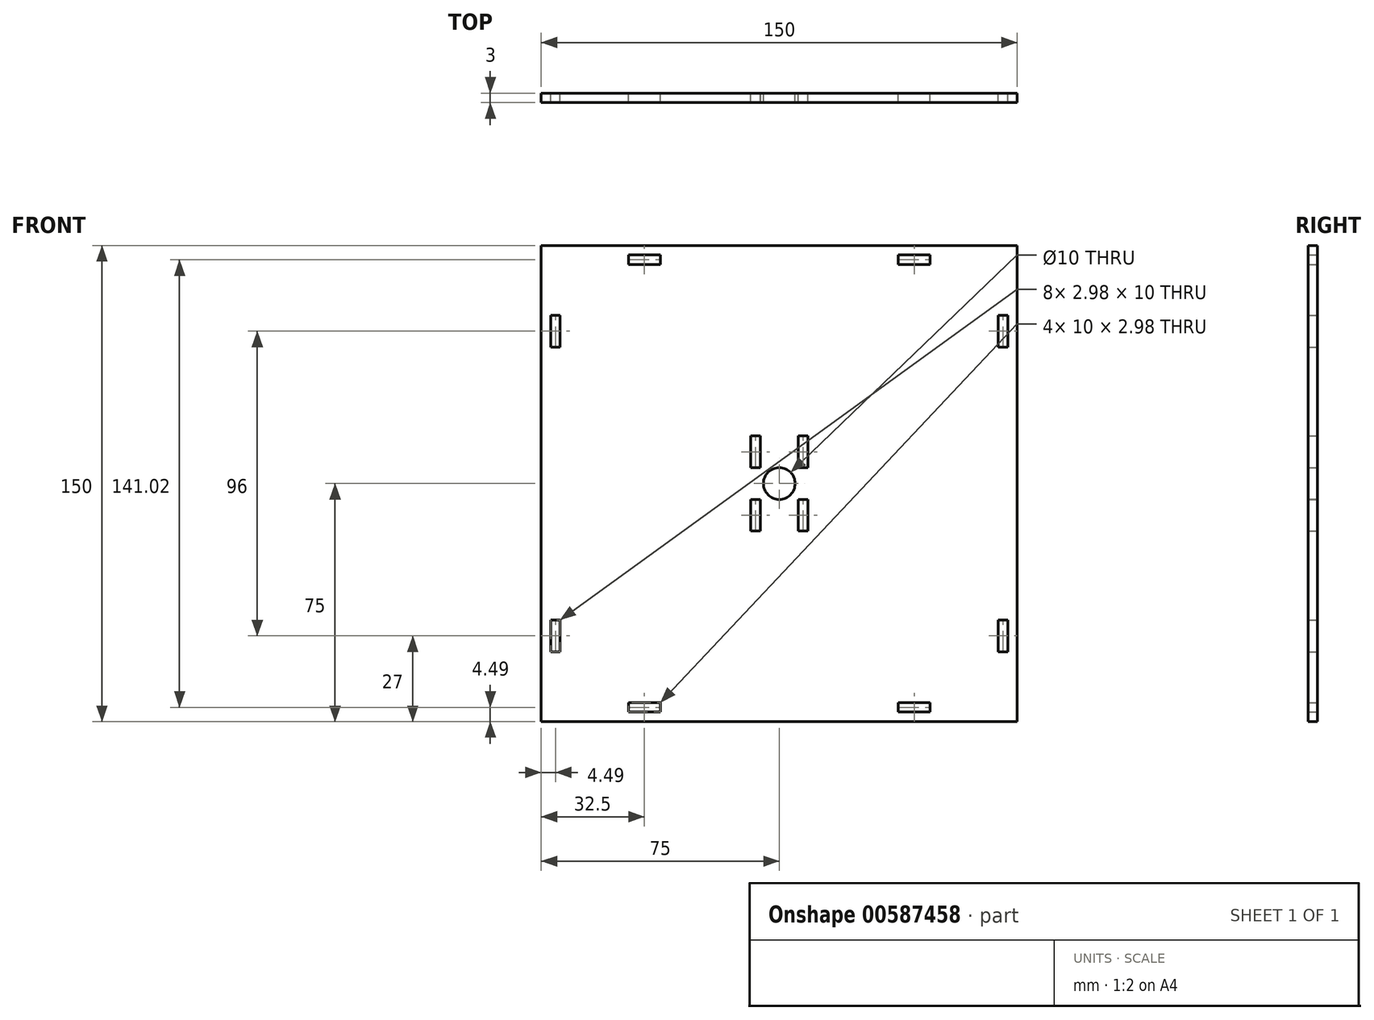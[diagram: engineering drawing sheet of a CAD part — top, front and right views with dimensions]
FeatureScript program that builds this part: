
annotation { "Feature Type Name" : "Feature", "Feature Type Description" : "" }
export const myFeature = defineFeature(function(context is Context, id is Id, definition is map)
    precondition{}
    {
        {
            var Q0;
            Q0=qCreatedBy(makeId("Front.planeOp"),FACE);
            var sketch = newSketch(context, id + "F0", { "sketchPlane" : qUnion([Q0])});
            skLineSegment(sketch, "E0.bottom", {"start": v(-75, 75) * mm, "end": v(75, 75) * mm});
            skLineSegment(sketch, "E0.top", {"start": v(-75, -75) * mm, "end": v(75, -75) * mm});
            skLineSegment(sketch, "E0.left", {"start": v(-75, 75) * mm, "end": v(-75, -75) * mm});
            skLineSegment(sketch, "E0.right", {"start": v(75, 75) * mm, "end": v(75, -75) * mm});
            skLineSegment(sketch, "E1.bottom", {"start": v(-47.5, 72) * mm, "end": v(-37.5, 72) * mm});
            skLineSegment(sketch, "E1.top", {"start": v(-47.5, 69.02) * mm, "end": v(-37.5, 69.02) * mm});
            skLineSegment(sketch, "E1.left", {"start": v(-47.5, 72) * mm, "end": v(-47.5, 69.02) * mm});
            skLineSegment(sketch, "E1.right", {"start": v(-37.5, 72) * mm, "end": v(-37.5, 69.02) * mm});
            skLineSegment(sketch, "E2", {"start": v(0, 75) * mm, "end": v(0, -75) * mm, "construction": true});
            skLineSegment(sketch, "E3", {"start": v(-75, 0) * mm, "end": v(75, 0) * mm, "construction": true});
            skLineSegment(sketch, "E4", {"start": v(-42.5, 72) * mm, "end": v(-42.5, 69.02) * mm, "construction": true});
            skLineSegment(sketch, "E5", {"start": v(-47.5, 70.5) * mm, "end": v(-37.5, 70.5) * mm, "construction": true});
            skLineSegment(sketch, "E6.MirrorCS", {"start": v(47.5, 72) * mm, "end": v(47.5, 69.02) * mm});
            skLineSegment(sketch, "E7.MirrorCS", {"start": v(37.5, 72) * mm, "end": v(37.5, 69.02) * mm});
            skLineSegment(sketch, "E8.MirrorCS", {"start": v(42.5, 72) * mm, "end": v(42.5, 69.02) * mm, "construction": true});
            skLineSegment(sketch, "E9.MirrorCS", {"start": v(47.5, 70.51) * mm, "end": v(37.5, 70.51) * mm, "construction": true});
            skLineSegment(sketch, "E10.MirrorCS", {"start": v(47.5, 69.02) * mm, "end": v(37.5, 69.02) * mm});
            skLineSegment(sketch, "E11.MirrorCS", {"start": v(47.5, 72) * mm, "end": v(37.5, 72) * mm});
            skLineSegment(sketch, "E12.MirrorCS", {"start": v(47.5, -70.5) * mm, "end": v(37.5, -70.5) * mm, "construction": true});
            skLineSegment(sketch, "E13.MirrorCS", {"start": v(42.5, -72) * mm, "end": v(42.5, -69.02) * mm, "construction": true});
            skLineSegment(sketch, "E14.MirrorCS", {"start": v(47.5, -72) * mm, "end": v(37.5, -72) * mm});
            skLineSegment(sketch, "E15.MirrorCS", {"start": v(37.5, -72) * mm, "end": v(37.5, -69.02) * mm});
            skLineSegment(sketch, "E16.MirrorCS", {"start": v(47.5, -72) * mm, "end": v(47.5, -69.02) * mm});
            skLineSegment(sketch, "E17.MirrorCS", {"start": v(47.5, -69.02) * mm, "end": v(37.5, -69.02) * mm});
            skLineSegment(sketch, "E18.MirrorCS", {"start": v(-47.5, -70.5) * mm, "end": v(-37.5, -70.5) * mm, "construction": true});
            skLineSegment(sketch, "E19.MirrorCS", {"start": v(-47.5, -72) * mm, "end": v(-37.5, -72) * mm});
            skLineSegment(sketch, "E20.MirrorCS", {"start": v(-47.5, -72) * mm, "end": v(-47.5, -69.02) * mm});
            skLineSegment(sketch, "E21.MirrorCS", {"start": v(-47.5, -69.02) * mm, "end": v(-37.5, -69.02) * mm});
            skLineSegment(sketch, "E22.MirrorCS", {"start": v(-42.5, -72) * mm, "end": v(-42.5, -69.02) * mm, "construction": true});
            skLineSegment(sketch, "E23.MirrorCS", {"start": v(-37.5, -72) * mm, "end": v(-37.5, -69.02) * mm});
            skLineSegment(sketch, "E24.bottom", {"start": v(-72, 53) * mm, "end": v(-69.02, 53) * mm});
            skLineSegment(sketch, "E24.top", {"start": v(-72, 43) * mm, "end": v(-69.02, 43) * mm});
            skLineSegment(sketch, "E24.left", {"start": v(-72, 53) * mm, "end": v(-72, 43) * mm});
            skLineSegment(sketch, "E24.right", {"start": v(-69.02, 53) * mm, "end": v(-69.02, 43) * mm});
            skLineSegment(sketch, "E25", {"start": v(-70.51, 53) * mm, "end": v(-70.51, 43) * mm, "construction": true});
            skLineSegment(sketch, "E26", {"start": v(-72, 48) * mm, "end": v(-69.02, 48) * mm, "construction": true});
            skLineSegment(sketch, "E27.MirrorCS", {"start": v(70.51, 53) * mm, "end": v(70.51, 43) * mm, "construction": true});
            skLineSegment(sketch, "E28.MirrorCS", {"start": v(72, 53) * mm, "end": v(72, 43) * mm});
            skLineSegment(sketch, "E29.MirrorCS", {"start": v(72, 43) * mm, "end": v(69.02, 43) * mm});
            skLineSegment(sketch, "E30.MirrorCS", {"start": v(72, 53) * mm, "end": v(69.02, 53) * mm});
            skLineSegment(sketch, "E31.MirrorCS", {"start": v(72, 48) * mm, "end": v(69.02, 48) * mm, "construction": true});
            skLineSegment(sketch, "E32.MirrorCS", {"start": v(69.02, 53) * mm, "end": v(69.02, 43) * mm});
            skLineSegment(sketch, "E33.MirrorCS", {"start": v(72, -43) * mm, "end": v(69.02, -43) * mm});
            skLineSegment(sketch, "E34.MirrorCS", {"start": v(72, -53) * mm, "end": v(69.02, -53) * mm});
            skLineSegment(sketch, "E35.MirrorCS", {"start": v(69.02, -53) * mm, "end": v(69.02, -43) * mm});
            skLineSegment(sketch, "E36.MirrorCS", {"start": v(70.51, -53) * mm, "end": v(70.51, -43) * mm, "construction": true});
            skLineSegment(sketch, "E37.MirrorCS", {"start": v(72, -53) * mm, "end": v(72, -43) * mm});
            skLineSegment(sketch, "E38.MirrorCS", {"start": v(72, -48) * mm, "end": v(69.02, -48) * mm, "construction": true});
            skLineSegment(sketch, "E39.MirrorCS", {"start": v(-72, -48) * mm, "end": v(-69.02, -48) * mm, "construction": true});
            skLineSegment(sketch, "E40.MirrorCS", {"start": v(-72, -43) * mm, "end": v(-69.02, -43) * mm});
            skLineSegment(sketch, "E41.MirrorCS", {"start": v(-69.02, -53) * mm, "end": v(-69.02, -43) * mm});
            skLineSegment(sketch, "E42.MirrorCS", {"start": v(-70.51, -53) * mm, "end": v(-70.51, -43) * mm, "construction": true});
            skLineSegment(sketch, "E43.MirrorCS", {"start": v(-72, -53) * mm, "end": v(-72, -43) * mm});
            skLineSegment(sketch, "E44.MirrorCS", {"start": v(-72, -53) * mm, "end": v(-69.02, -53) * mm});
            skLineSegment(sketch, "E45.MirrorCS", {"start": v(-6, 5) * mm, "end": v(-8.98, 5) * mm});
            skLineSegment(sketch, "E46.MirrorCS", {"start": v(-6, -5) * mm, "end": v(-8.98, -5) * mm});
            skLineSegment(sketch, "E47.MirrorCS", {"start": v(6, -5) * mm, "end": v(8.98, -5) * mm});
            skLineSegment(sketch, "E48.MirrorCS", {"start": v(6, 5) * mm, "end": v(8.98, 5) * mm});
            skPoint(sketch, "E49.endSnap0", {"position": v(-7.54, -5) * mm});
            skCircle(sketch, "E50", {"center": v(0, 0) * mm, "radius": 5 * mm});
            skLineSegment(sketch, "E51", {"start": v(-8.98, -5) * mm, "end": v(-8.98, -15) * mm});
            skLineSegment(sketch, "E52", {"start": v(-8.98, -15) * mm, "end": v(-6, -15) * mm});
            skLineSegment(sketch, "E53", {"start": v(-6, -15) * mm, "end": v(-6, -5) * mm});
            skLineSegment(sketch, "E54", {"start": v(6, -5) * mm, "end": v(6, -15) * mm});
            skLineSegment(sketch, "E55", {"start": v(6, -15) * mm, "end": v(8.98, -15) * mm});
            skLineSegment(sketch, "E56", {"start": v(8.98, -15) * mm, "end": v(8.98, -5) * mm});
            skLineSegment(sketch, "E57", {"start": v(6, 5) * mm, "end": v(6, 15) * mm});
            skLineSegment(sketch, "E58", {"start": v(6, 15) * mm, "end": v(8.98, 15) * mm});
            skLineSegment(sketch, "E59", {"start": v(8.98, 15) * mm, "end": v(8.98, 5) * mm});
            skLineSegment(sketch, "E60", {"start": v(-8.98, 5) * mm, "end": v(-8.98, 15) * mm});
            skLineSegment(sketch, "E61", {"start": v(-8.98, 15) * mm, "end": v(-6, 15) * mm});
            skLineSegment(sketch, "E62", {"start": v(-6, 15) * mm, "end": v(-6, 5) * mm});
            skSolve(sketch);
        }
        {
            var Q0;
            Q0 = qSketchRegion(id + "F0", true);
            extrude(context, id + "F1", {"entities" : qUnion([Q0]), "depth" : 3 * mm, "offsetDistance" : 25 * mm});
        }
    });
